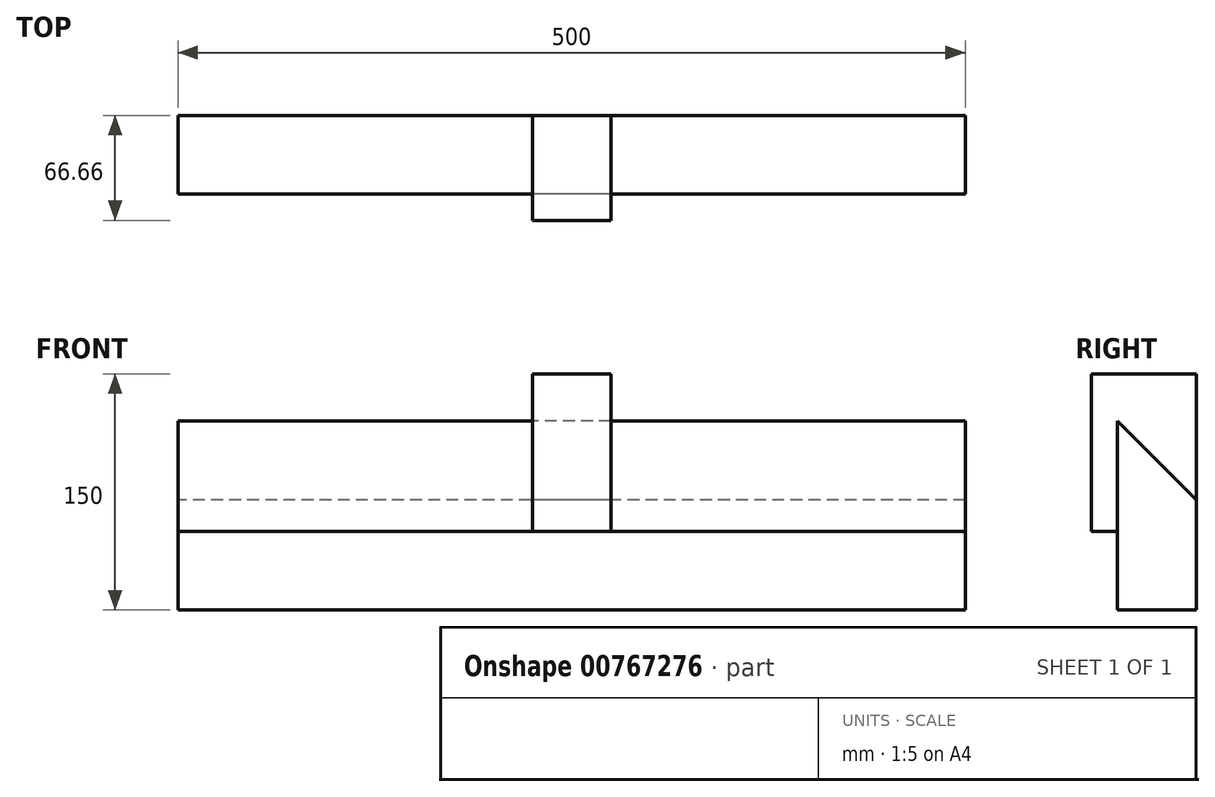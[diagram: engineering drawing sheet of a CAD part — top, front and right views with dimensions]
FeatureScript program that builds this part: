
annotation { "Feature Type Name" : "Feature", "Feature Type Description" : "" }
export const myFeature = defineFeature(function(context is Context, id is Id, definition is map)
    precondition{}
    {
        {
            var Q0;
            Q0=qCreatedBy(makeId("Right.planeOp"),FACE);
            var sketch = newSketch(context, id + "F0", { "sketchPlane" : qUnion([Q0])});
            skLineSegment(sketch, "E0.bottom", {"start": v(25, 75) * mm, "end": v(-25, 75) * mm});
            skLineSegment(sketch, "E0.top", {"start": v(25, -75) * mm, "end": v(-25, -75) * mm});
            skLineSegment(sketch, "E0.left", {"start": v(25, 75) * mm, "end": v(25, -75) * mm});
            skLineSegment(sketch, "E0.right", {"start": v(-25, 75) * mm, "end": v(-25, -75) * mm});
            skPoint(sketch, "E0.middle", {"position": v(0, 0) * mm});
            skLineSegment(sketch, "E1", {"start": v(-25, 45) * mm, "end": v(25, -5) * mm});
            skLineSegment(sketch, "E2.bottom", {"start": v(-24.98, 75) * mm, "end": v(-41.66, 75) * mm});
            skLineSegment(sketch, "E2.top", {"start": v(-24.98, -25) * mm, "end": v(-41.66, -25) * mm});
            skLineSegment(sketch, "E2.left", {"start": v(-24.98, 75) * mm, "end": v(-24.98, -25) * mm});
            skLineSegment(sketch, "E2.right", {"start": v(-41.66, 75) * mm, "end": v(-41.66, -25) * mm});
            skSolve(sketch);
        }
        {
            var Q0;
            {var subQ5=sQuery(id+"F0.wireOp",EDGE,"E0.top");Q0=makeQuery(id+"F0.imprint","IMPRINT",FACE,{"disambiguationData":[TD([[makeQuery(id+"F0.imprint","IMPRINT",EDGE,{"derivedFrom":subQ5}),-1.0]])]});}
            extrude(context, id + "F1", {"entities" : qUnion([Q0]), "endBound" : BoundingType.SYMMETRIC, "depth" : 500 * mm, "offsetDistance" : 25 * mm});
        }
        {
            var Q0;
            {var subQ0=sQuery(id+"F0.wireOp",EDGE,"E0.bottom");Q0=makeQuery(id+"F0.imprint","IMPRINT",FACE,{"disambiguationData":[TD([[makeQuery(id+"F0.imprint","IMPRINT",EDGE,{"derivedFrom":subQ0}),1.0]])]});}
            var Q1;
            {var subQ0=sQuery(id+"F0.wireOp",EDGE,"E2.right");Q1=makeQuery(id+"F0.imprint","IMPRINT",FACE,{"disambiguationData":[TD([[makeQuery(id+"F0.imprint","IMPRINT",EDGE,{"derivedFrom":subQ0}),1.0]])]});}
            extrude(context, id + "F2", {"entities" : qUnion([Q0, Q1]), "endBound" : BoundingType.SYMMETRIC, "depth" : 50 * mm, "offsetDistance" : 25 * mm});
        }
    });
